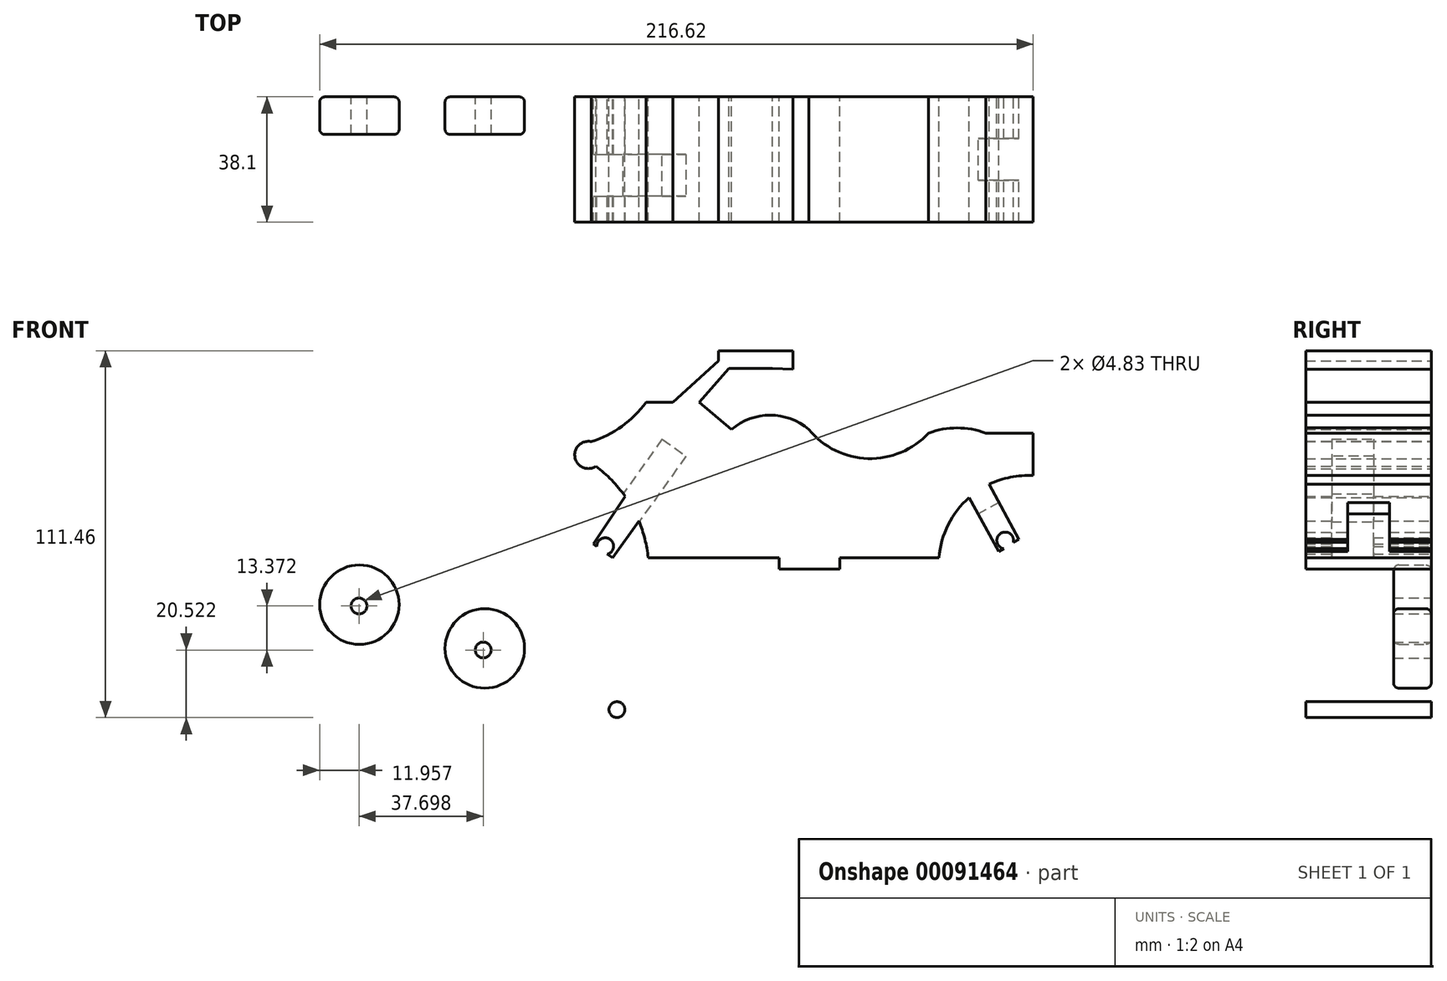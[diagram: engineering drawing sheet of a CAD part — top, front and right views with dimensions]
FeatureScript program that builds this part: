
annotation { "Feature Type Name" : "Feature", "Feature Type Description" : "" }
export const myFeature = defineFeature(function(context is Context, id is Id, definition is map)
    precondition{}
    {
        {
            var Q0;
            Q0=qCreatedBy(makeId("Front.planeOp"),FACE);
            cPlane(context, id + "F0", {"entities" : qUnion([Q0]), "cplaneType" : CPlaneType.OFFSET, "offset" : 38.1 * mm, "width" : 152.4 * mm, "height" : 152.4 * mm});
        }
        {
            var Q0;
            Q0=qCreatedBy(id+"F0.planeOp",FACE);
            var sketch = newSketch(context, id + "F1", { "sketchPlane" : qUnion([Q0])});
            skArc(sketch, "E0", {"start": v(0, 38.96) * mm, "mid": v(17.94, 30.17) * mm, "end": v(36.35, 37.92) * mm});
            skArc(sketch, "E1", {"start": v(0, 38.96) * mm, "mid": v(-11.73, 43.33) * mm, "end": v(-23.46, 38.96) * mm});
            skLineSegment(sketch, "E2", {"start": v(-23.46, 38.96) * mm, "end": v(-33.22, 47.31) * mm});
            skLineSegment(sketch, "E3", {"start": v(-33.22, 47.31) * mm, "end": v(-49.43, 47.31) * mm});
            skArc(sketch, "E4", {"start": v(-66, 35.3) * mm, "mid": v(-56.74, 39.95) * mm, "end": v(-49.43, 47.31) * mm});
            skArc(sketch, "E5", {"start": v(-48.75, 0) * mm, "mid": v(-53.77, 15.59) * mm, "end": v(-64.69, 27.79) * mm});
            skLineSegment(sketch, "E6", {"start": v(-48.75, 0) * mm, "end": v(39.48, 0) * mm});
            skLineSegment(sketch, "E7", {"start": v(-33.22, 47.31) * mm, "end": v(-24.3, 57.49) * mm});
            skLineSegment(sketch, "E8", {"start": v(-24.3, 57.49) * mm, "end": v(-11.02, 57.49) * mm});
            skLineSegment(sketch, "E9", {"start": v(-11.02, 57.49) * mm, "end": v(-11.02, 62.94) * mm});
            skLineSegment(sketch, "E10", {"start": v(-11.02, 62.94) * mm, "end": v(-27.38, 62.94) * mm});
            skLineSegment(sketch, "E11", {"start": v(-27.38, 59.86) * mm, "end": v(-27.38, 62.94) * mm});
            skLineSegment(sketch, "E12", {"start": v(-11.02, 62.94) * mm, "end": v(-4.86, 62.94) * mm});
            skLineSegment(sketch, "E13", {"start": v(-4.86, 62.94) * mm, "end": v(-4.86, 57.25) * mm});
            skArc(sketch, "E14", {"start": v(53.68, 37.92) * mm, "mid": v(45.02, 39.47) * mm, "end": v(36.35, 37.92) * mm});
            skLineSegment(sketch, "E15", {"start": v(-11.02, 57.49) * mm, "end": v(-4.86, 57.25) * mm});
            skLineSegment(sketch, "E16", {"start": v(-27.38, 59.86) * mm, "end": v(-41.33, 47.31) * mm});
            skLineSegment(sketch, "E17", {"start": v(53.68, 37.92) * mm, "end": v(68.12, 37.92) * mm});
            skLineSegment(sketch, "E18", {"start": v(68.12, 37.92) * mm, "end": v(68.12, 24.97) * mm});
            skArc(sketch, "E19", {"start": v(68.12, 24.97) * mm, "mid": v(48.69, 18.35) * mm, "end": v(39.48, 0) * mm});
            skLineSegment(sketch, "E20", {"start": v(-9, 0) * mm, "end": v(-9, -3.4) * mm});
            skLineSegment(sketch, "E21", {"start": v(-9, -3.4) * mm, "end": v(9.34, -3.4) * mm});
            skLineSegment(sketch, "E22", {"start": v(9.34, -3.4) * mm, "end": v(9.34, 0) * mm});
            skLineSegment(sketch, "E23", {"start": v(-64.69, 27.79) * mm, "end": v(-66, 35.3) * mm});
            skLineSegment(sketch, "E24", {"start": v(48.69, 18.35) * mm, "end": v(57.71, 1.93) * mm});
            skLineSegment(sketch, "E25", {"start": v(-48.75, 0) * mm, "end": v(-51.72, 0) * mm});
            skLineSegment(sketch, "E26", {"start": v(-55.78, 18.74) * mm, "end": v(-65.46, 4.18) * mm});
            skLineSegment(sketch, "E27", {"start": v(-51.6, 11.2) * mm, "end": v(-59.6, 0) * mm});
            skLineSegment(sketch, "E28", {"start": v(54.7, 22.32) * mm, "end": v(63.74, 5.58) * mm});
            skLineSegment(sketch, "E29", {"start": v(-59.6, 0) * mm, "end": v(-61.16, 1.11) * mm});
            skLineSegment(sketch, "E30", {"start": v(-64.35, 3.39) * mm, "end": v(-65.46, 4.18) * mm});
            skArc(sketch, "E31", {"start": v(-61.16, 1.11) * mm, "mid": v(-60.34, 5.63) * mm, "end": v(-64.35, 3.39) * mm});
            skLineSegment(sketch, "E32", {"start": v(57.71, 1.93) * mm, "end": v(59.22, 2.76) * mm});
            skPoint(sketch, "E32.endSnap0", {"position": v(59.22, 13.95) * mm});
            skArc(sketch, "E33", {"start": v(62.07, 4.68) * mm, "mid": v(58.19, 7.38) * mm, "end": v(59.22, 2.76) * mm});
            skLineSegment(sketch, "E34", {"start": v(62.07, 4.68) * mm, "end": v(63.74, 5.58) * mm});
            skArc(sketch, "E35", {"start": v(-66, 35.3) * mm, "mid": v(-71, 30.54) * mm, "end": v(-64.69, 27.79) * mm});
            skSolve(sketch);
        }
        {
            var Q0;
            Q0 = qSketchRegion(id + "F1", true);
            extrude(context, id + "F2", {"entities" : qUnion([Q0]), "depth" : 38.1 * mm});
        }
        {
            var Q0;
            Q0=makeQuery(id+"F2.opExtrude","SWEPT_FACE",FACE,{"disambiguationData":[OSD([sQuery(id+"F1.wireOp",EDGE,"E34")])]});
            var sketch = newSketch(context, id + "F3", { "sketchPlane" : qUnion([Q0])});
            skLineSegment(sketch, "E36.bottom", {"start": v(58.75, 57.15) * mm, "end": v(51.13, 57.15) * mm});
            skLineSegment(sketch, "E36.top", {"start": v(58.75, 50.8) * mm, "end": v(51.13, 50.8) * mm});
            skLineSegment(sketch, "E36.left", {"start": v(58.75, 57.15) * mm, "end": v(58.75, 50.8) * mm});
            skLineSegment(sketch, "E36.right", {"start": v(51.13, 57.15) * mm, "end": v(51.13, 50.8) * mm});
            skLineSegment(sketch, "E37.top", {"start": v(58.75, 63.5) * mm, "end": v(51.13, 63.5) * mm});
            skLineSegment(sketch, "E37.left", {"start": v(58.75, 57.15) * mm, "end": v(58.75, 63.5) * mm});
            skLineSegment(sketch, "E37.right", {"start": v(51.13, 57.15) * mm, "end": v(51.13, 63.5) * mm});
            skSolve(sketch);
        }
        {
            var Q0;
            Q0 = qSketchRegion(id + "F3", true);
            extrude(context, id + "F4", {"entities" : qUnion([Q0]), "operationType" : NewBodyOperationType.REMOVE, "oppositeDirection" : true, "depth" : 12.7 * mm});
        }
        {
            var Q0;
            Q0 = qSketchRegion(id + "F3", true);
            extrude(context, id + "F5", {"entities" : qUnion([Q0]), "operationType" : NewBodyOperationType.REMOVE, "oppositeDirection" : true, "depth" : 12.7 * mm, "hasSecondDirection" : true, "secondDirectionOppositeDirection" : false, "secondDirectionDepth" : 2.54 * mm});
        }
        {
            var Q0;
            Q0=qCreatedBy(id+"F0.planeOp",FACE);
            var sketch = newSketch(context, id + "F6", { "sketchPlane" : qUnion([Q0])});
            skCircle(sketch, "E38", {"center": v(-98.37, -27.52) * mm, "radius": 12.06 * mm});
            skSolve(sketch);
        }
        {
            var Q0;
            Q0=qCreatedBy(makeId("Top.planeOp"),FACE);
            var sketch = newSketch(context, id + "F7", { "sketchPlane" : qUnion([Q0])});
            skLineSegment(sketch, "E39", {"start": v(-62.45, -60.28) * mm, "end": v(-62.45, -53.93) * mm});
            skLineSegment(sketch, "E40", {"start": v(-54.83, -53.93) * mm, "end": v(-62.45, -53.93) * mm});
            skLineSegment(sketch, "E41", {"start": v(-54.83, -53.93) * mm, "end": v(-54.83, -60.28) * mm});
            skLineSegment(sketch, "E42", {"start": v(-62.45, -60.28) * mm, "end": v(-54.83, -60.28) * mm});
            skLineSegment(sketch, "E43.left", {"start": v(-62.45, -53.93) * mm, "end": v(-62.45, -47.58) * mm});
            skLineSegment(sketch, "E44", {"start": v(-62.45, -47.58) * mm, "end": v(-54.87, -47.58) * mm});
            skLineSegment(sketch, "E45", {"start": v(-54.87, -47.58) * mm, "end": v(-54.83, -53.93) * mm});
            skSolve(sketch);
        }
        {
            var Q0;
            Q0 = qSketchRegion(id + "F7", true);
            extrude(context, id + "F8", {"entities" : qUnion([Q0]), "operationType" : NewBodyOperationType.REMOVE, "oppositeDirection" : true, "depth" : 25.4 * mm});
        }
        {
            var Q0;
            Q0 = qSketchRegion(id + "F6", true);
            extrude(context, id + "F9", {"entities" : qUnion([Q0]), "depth" : 11.43 * mm});
        }
        {
            var Q0;
            Q0 = qSketchRegion(id + "F6", true);
            extrude(context, id + "F10", {"entities" : qUnion([Q0]), "operationType" : NewBodyOperationType.ADD, "depth" : 11.43 * mm});
        }
        {
            var Q0;
            Q0=makeQuery(id+"F9.opExtrude","CAP_FACE",FACE,{"disambiguationData":[OSD([sQuery(id+"F6.wireOp",EDGE,"E38")])],"isStart":false});
            fillet(context, id + "F11", {"entities" : qUnion([Q0]), "radius" : 1.57 * mm, "tangentPropagation" : true, "allowEdgeOverflow" : false});
        }
        {
            var Q0;
            Q0=makeQuery(id+"F9.opExtrude","CAP_FACE",FACE,{"disambiguationData":[OSD([sQuery(id+"F6.wireOp",EDGE,"E38")])],"isStart":true});
            fillet(context, id + "F12", {"entities" : qUnion([Q0]), "radius" : 1.59 * mm, "tangentPropagation" : true, "allowEdgeOverflow" : false});
        }
        {
            var Q0;
            Q0 = qSketchRegion(id + "F7", true);
            extrude(context, id + "F13", {"entities" : qUnion([Q0]), "operationType" : NewBodyOperationType.REMOVE, "oppositeDirection" : true, "depth" : 12.7 * mm});
        }
        {
            var Q0;
            Q0=qCreatedBy(id+"F0.planeOp",FACE);
            var sketch = newSketch(context, id + "F14", { "sketchPlane" : qUnion([Q0])});
            skCircle(sketch, "E46", {"center": v(-58.25, -46.1) * mm, "radius": 2.41 * mm});
            skSolve(sketch);
        }
        {
            var Q0;
            Q0 = qSketchRegion(id + "F14", true);
            extrude(context, id + "F15", {"entities" : qUnion([Q0]), "depth" : 38.1 * mm});
        }
        {
            var Q0;
            Q0=makeQuery(id+"F2.opExtrude","SWEPT_FACE",FACE,{"disambiguationData":[OSD([sQuery(id+"F1.wireOp",EDGE,"E30")])]});
            var sketch = newSketch(context, id + "F16", { "sketchPlane" : qUnion([Q0])});
            skLineSegment(sketch, "E47.bottom", {"start": v(-57.18, 55.61) * mm, "end": v(-48.3, 55.61) * mm});
            skLineSegment(sketch, "E47.top", {"start": v(-57.18, 61.96) * mm, "end": v(-48.3, 61.96) * mm});
            skLineSegment(sketch, "E47.right", {"start": v(-48.3, 55.61) * mm, "end": v(-48.3, 61.96) * mm});
            skPoint(sketch, "E48", {"position": v(-55.7, 23.54) * mm});
            skLineSegment(sketch, "E49", {"start": v(-57.18, 61.96) * mm, "end": v(-57.18, 55.61) * mm});
            skLineSegment(sketch, "E50", {"start": v(-57.18, 61.96) * mm, "end": v(-57.18, 68.31) * mm});
            skLineSegment(sketch, "E51", {"start": v(-48.3, 61.96) * mm, "end": v(-48.3, 68.31) * mm});
            skLineSegment(sketch, "E52", {"start": v(-57.18, 68.31) * mm, "end": v(-48.3, 68.31) * mm});
            skSolve(sketch);
        }
        {
            var Q0;
            Q0 = qSketchRegion(id + "F16", true);
            extrude(context, id + "F17", {"entities" : qUnion([Q0]), "operationType" : NewBodyOperationType.REMOVE, "oppositeDirection" : true, "depth" : 38.1 * mm});
        }
        {
            var Q0;
            Q0=qCreatedBy(id+"F0.planeOp",FACE);
            var sketch = newSketch(context, id + "F18", { "sketchPlane" : qUnion([Q0])});
            skCircle(sketch, "E53", {"center": v(-136.44, -14.24) * mm, "radius": 12.07 * mm});
            skSolve(sketch);
        }
        {
            var Q0;
            Q0=makeQuery(id+"F18.imprint","IMPRINT",FACE,{"disambiguationData":[TD([[makeQuery(id+"F18.imprint","IMPRINT",EDGE,{"derivedFrom":sQuery(id+"F18.wireOp",EDGE,"E53")}),1.0]])]});
            extrude(context, id + "F19", {"entities" : qUnion([Q0]), "depth" : 11.43 * mm});
        }
        {
            var Q0;
            Q0 = qSketchRegion(id + "F16", true);
            extrude(context, id + "F20", {"entities" : qUnion([Q0]), "operationType" : NewBodyOperationType.REMOVE, "oppositeDirection" : true, "depth" : 38.1 * mm});
        }
        {
            var Q0;
            Q0=makeQuery(id+"F19.opExtrude","CAP_EDGE",EDGE,{"disambiguationData":[OSD([sQuery(id+"F18.wireOp",EDGE,"E53")])],"isStart":true});
            var Q1;
            Q1=makeQuery(id+"F19.opExtrude","CAP_EDGE",EDGE,{"disambiguationData":[OSD([sQuery(id+"F18.wireOp",EDGE,"E53")])],"isStart":false});
            fillet(context, id + "F21", {"entities" : qUnion([Q0, Q1]), "radius" : 1.6 * mm, "tangentPropagation" : true, "allowEdgeOverflow" : false});
        }
        {
            var Q0;
            Q0=qCreatedBy(id+"F0.planeOp",FACE);
            var sketch = newSketch(context, id + "F22", { "sketchPlane" : qUnion([Q0])});
            skCircle(sketch, "E54", {"center": v(-136.54, -14.63) * mm, "radius": 2.41 * mm});
            skSolve(sketch);
        }
        {
            var Q0;
            Q0=makeQuery(id+"F22.imprint","IMPRINT",FACE,{"disambiguationData":[TD([[makeQuery(id+"F22.imprint","IMPRINT",EDGE,{"derivedFrom":sQuery(id+"F22.wireOp",EDGE,"E54")}),1.0]])]});
            extrude(context, id + "F23", {"entities" : qUnion([Q0]), "operationType" : NewBodyOperationType.REMOVE, "depth" : 25.4 * mm});
        }
        {
            var Q0;
            Q0=qCreatedBy(makeId("Front.planeOp"),FACE);
            var sketch = newSketch(context, id + "F24", { "sketchPlane" : qUnion([Q0])});
            skCircle(sketch, "E55", {"center": v(-98.85, -28) * mm, "radius": 2.41 * mm});
            skSolve(sketch);
        }
        {
            var Q0;
            Q0 = qSketchRegion(id + "F24", true);
            extrude(context, id + "F25", {"entities" : qUnion([Q0]), "operationType" : NewBodyOperationType.REMOVE, "depth" : 50.8 * mm});
        }
    });
